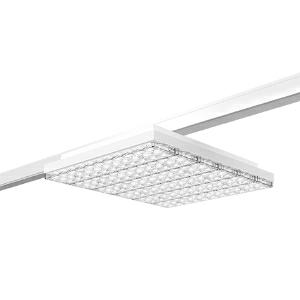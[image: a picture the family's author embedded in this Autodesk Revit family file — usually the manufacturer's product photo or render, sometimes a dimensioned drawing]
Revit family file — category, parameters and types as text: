
# Revit family: 3f_filippi_-_3f_six_blindo_ugr_3f_filippi_-_47713_-_3f_six_wh_40-840_dali_ugr_307x378
name_source: partatom
category: Lighting Fixtures
units: mm (PartAtom-declared; Revit-internal decimal feet)

## family parameters
Cut with Voids When Loaded = No
Host = Face
Light Source = No
Part Type = Normal
Room Calculation Point = No
Round Connector Dimension = Use Diameter
Shared = No

## types (1)
- 3F Filippi - 3F Six Blindo UGR (1 x LED, 6914 lm, 40 W, 4000 K)
    Apparent Load = 40 VA
    Approval mark = CE
    CIE Flux Codes = 83 96 99 97 100
    Color Rendering = 80
    Color Temperature = 4000 K
    Control Gear = Electronic transformer
    Default Elevation = 1800 mm
    Description = ILLUMINOTECHNICAL
Luminous efficiency 100% (DLOR 98%, ULOR 2%).
Initial luminous flux of the luminaire 6914 lm.
Controlled direct symmetric distribution.
Installation Interdistance Transv.D = 1.39 x hu - Long.D = 1.30 x hu.
Average luminance <3000 cd/m² for radial angles >65°.
Tabular UGR (CIE 117 - 4H-8H; S=0.25H; 70/50/20): RUG 19.1 - 16.9.
Beam angle: 78° - 75°.
Luminous efficacy 173 lm/W.
Lifetime (L93/B10): 30000 h. (tq+25°C)
Lifetime (L90/B10): 50000 h. (tq+25°C)
Lifetime (L85/B10): 80000 h. (tq+25°C)
Lifetime (L80/B10): 100000 h. (tq+25°C)
Lifetime (L85/B10): 50000 h. (tq+50°C)
Sudden decreased luminous flux after 50000 hours: 0% (C0).
Photobiological safety in compliance with IEC/TR 62778: RG0 risk exempt, (IEC 62471).
In compliance with IEC/EN 62722-2-1 - IEC/EN 62717 standards.

SOURCE
Linear LED module 40W/840.
Energy efficiency class (UE 2019/2020 - UE 2019/2015): C.
CIE 13.3 Colour rendering index: CRI >80 (R9 <50%).
IES TM-30 Fidelity Index: Rf = 84 Rg = 95.
CCT nominal colour temperature 4000 K.
Colour initial tolerance (MacAdam): SDCM 3.

MECHANICAL
Housing in galvannealed steel, painted in white epoxy-polyester.
Transparent methacrylate (PMMA) controlled distribution lenses with flat external surface.
Luminaire with limited surface temperature. - D - (EN 60598-2-24)
Dimensions: 307x378 mm, height 52 mm. Weight 3.19 kg.
IP40 protection degree.
Mechanical strength to impacts IK06 (1 joule).
Glow-wire test resistance 650°C.

ELECTRICAL
Halogen Free DALI-2, PUSH-DIM, electronic wiring 230V-50/60Hz, power factor 0.95 at full load, THD <25%, constant output current, class I, 1 driver, 1 DALI addresse.
Power of the luminaire 40 W.
ENEC - CE.
SAFE FLICKER: PstLM=<1 and SVM=<0.4 (IEC TR 61547-1 and IEC TR 63158), to ensure a more comfortable and safe light.
Luminaire compliant with EN 60598-2-22 for power supply from a centralised emergency system CPSS (Central Power Supply System), not incorporated in the luminaire - high risk areas excluded. The default power and flux are 100% in AC and 15% in DC.
Ambient temperature from 0°C to +50°C.
Temperature class T6 max 85°C.
Power cable protrudes by 1 m with sheared end.
Relative humidity UR: <85%.

INSTALLATION
Ceiling / Suspended / Wall.

APPLICATIONS
Suitable product for food production plants (HACCP), IFS (Food Version 6), BRC (GSFS Food Version 7).
In commercial environments, exhibition areas, shops and stores.
In environments with VDTs, managerial offices and staterooms, public offices and schools.

LIGHT MANAGEMENT
Recommended minimum setting: 10%.
The device, equipped with DALI-2 driver, can be controlled manually with 3F Easy Dim technology or automatically/manually with 3F Smart Dimming technology and/or centralised DALI systems.
DALI-2 certification guarantees interoperability with other devices with the same certification.
In electrical systems without a regulation system (manual or automatic) and DALI bus, a suitable jumper must be made on the DA-DA terminals of the appliance.

WARNING
Luminaire designed for disposal/recycling at end-of-life.
Replaceable (LED only) light source by a professional. Replaceable control gear by a professional.
    Height = 52 mm  [stored 0.170604 ft]
    Lamp = 1 x LED
    Lamp Light Flux = 6914 lm
    Lamp Power = 40 W
    Lamp count = 1
    Length = 307 mm
    Lifetime = 50000 h
    Luminous efficacy = 173 lm/W
    Manufacturer = 3F Filippi
    ModVariant = No
    Model = 3F Filippi - 47713 - 3F Six WH 40-840 DALI UGR 307x378
    Mounting Place = Ceiling
    Mounting Type = Pendant
    Number of Poles = 1
    OnlyDefault = Yes
    Power Factor = 1
    Product Name = 3F Filippi - 3F Six Blindo UGR
    Product group = pendant luminaire
    ProductGroupID = 9
    Protection Class = Protection class I
    Protection Degree = IP 40
    RLX_Detail_Level = 1
    RLX_Emergency_Light_Flux = 0 lm
    RLX_Emergency_Type = 0
    RLX_Emergency_Type_DB = No
    RlxData = <blob elided: 71685 chars, md5=c906c754>
    Socket = socket
    Standby Power = 0 W
    System Light Flux = 6914 lm
    System Power = 40 W
    Type Comments = Product without accessories
    Type Image = 3ffilippi_3f_six_blindo.jpg
    URL = http://relux.com
    VarID = ---
    Voltage = 0 V
    Weight = 0.00 kg
    Width = 378 mm

note: [stored X ft] marks values corroborated as IEEE doubles in the binary element streams (Revit-internal decimal feet)

## geometry (parser evidence)
native form markers: Blend x4, Sweep x10
no freeform markers — native parametric forms only
